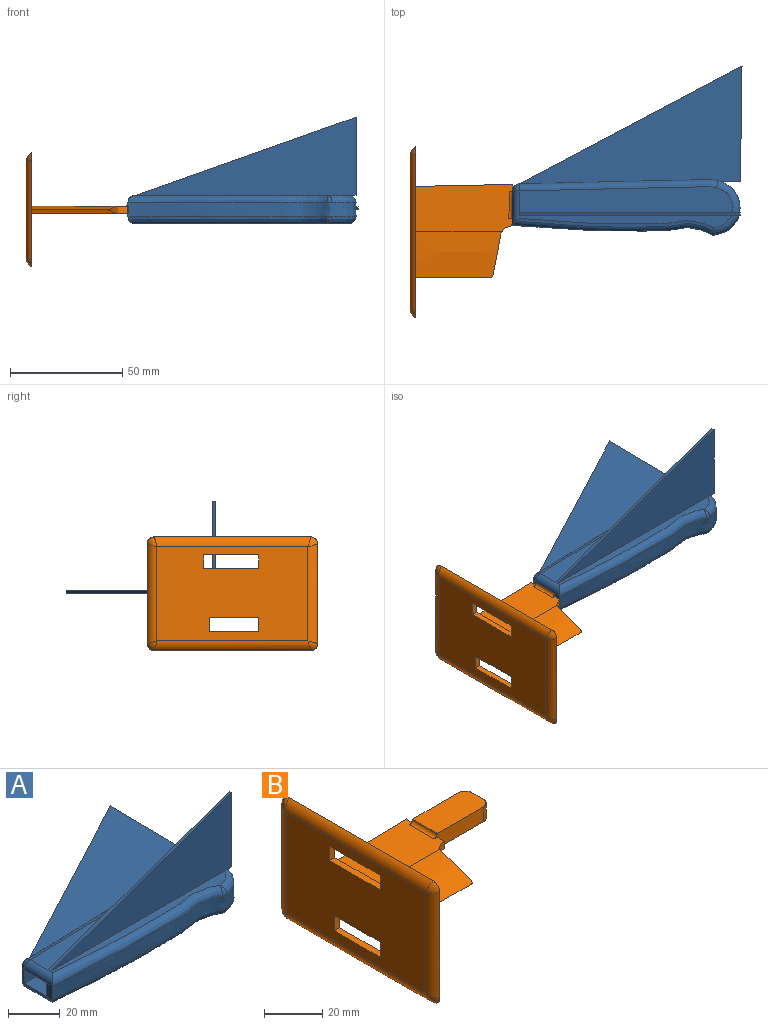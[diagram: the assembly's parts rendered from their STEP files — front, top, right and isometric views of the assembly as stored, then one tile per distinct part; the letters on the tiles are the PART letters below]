
ASSEMBLY  parts=2 mates=1
PART A: 35 faces, bbox 104.7x75.4x47.6 mm
  f0: extruded ~88.78x1.91mm, area 169.3mm2, adj f4,f10,f13,f33
  f1: plane 95.4x11.62mm, normal (0,0,1), area 1007.5mm2, adj f8,f10,f11,f28
  f2: extruded ~88.78x3.18mm, area 282.1mm2, adj f4,f13,f17,f34
  f3: plane 6.35x3.25mm, normal (-1,0.01,0), area 20.7mm2, adj f4,f11,f14,f22
  f4: extruded ~101.74x24.09mm, area 791mm2, adj f0,f2,f3,f7,f8,f9,f16,f18
  f5: plane 95.42x18.35mm, normal (0,0,-1), area 1418.4mm2, adj f14,f16,f17,f19
  f6: plane 94.75x5.46mm, normal (0,0,1), area 290.2mm2, adj f8,f9,f11,f29
  f7: bspline ~3.21x3.18mm, area 4.2mm2, adj f4,f8,f9
  f8: bspline ~24.16x12.16mm, area 155.7mm2, adj f1,f4,f6,f7,f10,f25
  f9: bspline ~90.69x7.29mm, area 439.3mm2, adj f4,f6,f7,f11
  f10: bspline ~94.66x5.16mm, area 441.7mm2, adj f0,f1,f8,f12
  f11: cylinder r=3.17mm len=15.4mm, axis (-0.01,-1,0), area 68.8mm2, adj f1,f3,f6,f9,f12,f23,f27
  f12: sphere r=3.17mm, area 27.2mm2, adj f10,f11,f13
  f13: cylinder r=3.17mm len=6.35mm, axis (0,0,1), area 31.2mm2, adj f0,f2,f12,f15,f20,f32
  f14: cylinder r=3.17mm len=15.4mm, axis (0.01,1,0), area 68.8mm2, adj f3,f5,f15,f16,f21
  f15: sphere r=3.17mm, area 21.4mm2, adj f13,f14,f17
  f16: bspline ~90.42x7.31mm, area 439.4mm2, adj f4,f5,f14,f18
  f17: bspline ~94.66x5.16mm, area 441.7mm2, adj f2,f5,f15,f19
  f18: bspline ~3.21x3.18mm, area 4.3mm2, adj f4,f16,f19
  f19: bspline ~24.11x11.95mm, area 155.6mm2, adj f4,f5,f17,f18
  f20: plane 25.4x6.35mm, normal (-0.01,-1,0), area 161.3mm2, adj f13,f21,f23,f24
  f21: plane 25.53x12.39mm, normal (0,0,1), area 307.8mm2, adj f14,f20,f22,f24
  f22: plane 25.4x6.35mm, normal (0.01,1,0), area 161.3mm2, adj f3,f21,f23,f24
  f23: plane 25.53x12.39mm, normal (0,0,-1), area 307.8mm2, adj f11,f20,f22,f24
  f24: plane 12.12x6.35mm, normal (-1,0.01,0), area 76.9mm2, adj f20,f21,f22,f23
  f25: plane 3.84x1.27mm, normal (0,0,-1), area 4.6mm2, adj f8,f26,f28,f29
  f26: plane 34.93x1.27mm, normal (1,0,0), area 44.4mm2, adj f25,f27,f28,f29
  f27: plane 98.59x34.93mm, normal (-0.33,0,0.94), area 132.8mm2, adj f11,f26,f28,f29
  f28: plane 98.57x34.93mm, normal (0,1,0), area 1721.6mm2, adj f1,f25,f26,f27
  f29: plane 98.59x34.93mm, normal (0,-1,0), area 1721.6mm2, adj f6,f25,f26,f27
  f30: plane 9.89x1.27mm, normal (-0.01,-1,0), area 12.6mm2, adj f4,f31,f33,f34
  f31: plane 51.45x1.27mm, normal (1,-0.01,0), area 65.3mm2, adj f30,f32,f33,f34
  f32: plane 99.38x52.57mm, normal (-0.47,0.88,0), area 142.8mm2, adj f13,f31,f33,f34
  f33: plane 99.39x52.58mm, normal (0,0,1), area 2494.7mm2, adj f0,f30,f31,f32
  f34: plane 99.38x52.57mm, normal (0,0,-1), area 2494.8mm2, adj f2,f30,f31,f32
PART B: 36 faces, bbox 71.2x76.2x50.8 mm
  f0: extruded ~43.31x3.18mm, area 137.5mm2, adj f1,f5,f7,f9
  f1: plane 3.18x1.78mm, normal (1,-0.01,0), area 5.7mm2, adj f0,f2,f7,f9
  f2: plane 3.18x1.35mm, normal (1,0,0), area 4.3mm2, adj f1,f7,f9,f13
  f3: cylinder r=1.52mm len=11.97mm, axis (-0.01,-1,0), area 28.6mm2, adj f9,f11,f13,f35
  f4: cylinder r=1.52mm len=11.97mm, axis (-0.01,-1,0), area 28.6mm2, adj f7,f11,f13,f34
  f5: plane 76.2x50.8mm, normal (1,0,0), area 3466.5mm2, adj f0,f7,f9,f14,f15,f18,f19,f20
  f6: plane 67.4x42mm, normal (-1,0,0), area 2541.2mm2, adj f19,f20,f23,f24,f26,f27,f28,f29
  f7: plane 43.31x20.92mm, normal (0,0,1), area 853.4mm2, adj f0,f1,f2,f4,f5,f8,f10,f11
  f8: extruded ~23.06x9.56mm, area 60.2mm2, adj f7,f9,f10,f14,f15
  f9: plane 43.31x20.92mm, normal (0,0,-1), area 853.4mm2, adj f0,f1,f2,f3,f5,f8,f10,f11
  f10: plane 3.39x3.18mm, normal (1,-0.01,0), area 10.8mm2, adj f7,f8,f9,f11
  f11: plane 23.9x6.23mm, normal (0,-1,0), area 140.2mm2, adj f3,f4,f7,f9,f10,f16,f34,f35
  f12: plane 6.22x5.59mm, normal (1,0,0), area 34.8mm2, adj f16,f17,f34,f35
  f13: plane 23.76x6.23mm, normal (0,1,0), area 139.3mm2, adj f2,f3,f4,f7,f9,f17,f34,f35
  f14: extruded ~38.72x20.64mm, area 753.3mm2, adj f5,f8,f9,f15
  f15: extruded ~38.72x20.64mm, area 753.3mm2, adj f5,f7,f8,f14
  f16: cylinder r=3.17mm len=6.22mm, axis (0,0,1), area 31mm2, adj f11,f12,f34,f35
  f17: cylinder r=3.17mm len=6.22mm, axis (0,0,-1), area 31mm2, adj f12,f13,f34,f35
  f18: bspline ~4.4x4.4mm, area 10.1mm2, adj f5,f19,f20
  f19: cylinder r=5.08mm len=69.85mm, axis (0,1,0), area 365.1mm2, adj f5,f6,f18,f21
  f20: cylinder r=5.08mm len=44.45mm, axis (0,0,1), area 229.9mm2, adj f5,f6,f18,f22
  f21: bspline ~4.4x4.4mm, area 10.1mm2, adj f5,f19,f23
  f22: bspline ~4.4x4.4mm, area 10.1mm2, adj f5,f20,f24
  f23: cylinder r=5.08mm len=44.45mm, axis (0,0,1), area 229.9mm2, adj f5,f6,f21,f25
  f24: cylinder r=5.08mm len=69.85mm, axis (0,1,0), area 365.1mm2, adj f5,f6,f22,f25
  f25: bspline ~4.4x4.4mm, area 10.1mm2, adj f5,f23,f24
  f26: plane 6.34x2.54mm, normal (0,-1,0), area 16.1mm2, adj f5,f6,f27,f29
  f27: plane 22.2x2.54mm, normal (0,0,-1), area 56.4mm2, adj f5,f6,f26,f28
  f28: plane 6.34x2.54mm, normal (0,1,0), area 16.1mm2, adj f5,f6,f27,f29
  f29: plane 22.2x2.54mm, normal (0,0,1), area 56.4mm2, adj f5,f6,f26,f28
  f30: plane 24.57x2.54mm, normal (0,0,1), area 62.4mm2, adj f5,f6,f31,f33
  f31: plane 6.07x2.54mm, normal (0,-1,0), area 15.4mm2, adj f5,f6,f30,f32
  f32: plane 24.57x2.54mm, normal (0,0,-1), area 62.4mm2, adj f5,f6,f31,f33
  f33: plane 6.07x2.54mm, normal (0,1,0), area 15.4mm2, adj f5,f6,f30,f32
  f34: plane 25.54x11.94mm, normal (0,0,1), area 299.7mm2, adj f4,f11,f12,f13,f16,f17
  f35: plane 25.54x11.94mm, normal (0,0,-1), area 299.7mm2, adj f3,f11,f12,f13,f16,f17
PLACE A t=(-50.88,25.81,-3.84)mm
PLACE B t=(-50.75,25.63,-3.91)mm
MATE planar A.f21 <-> B.f35  axis (0,0,1) through (-16.83,2.08,-7.02)mm
